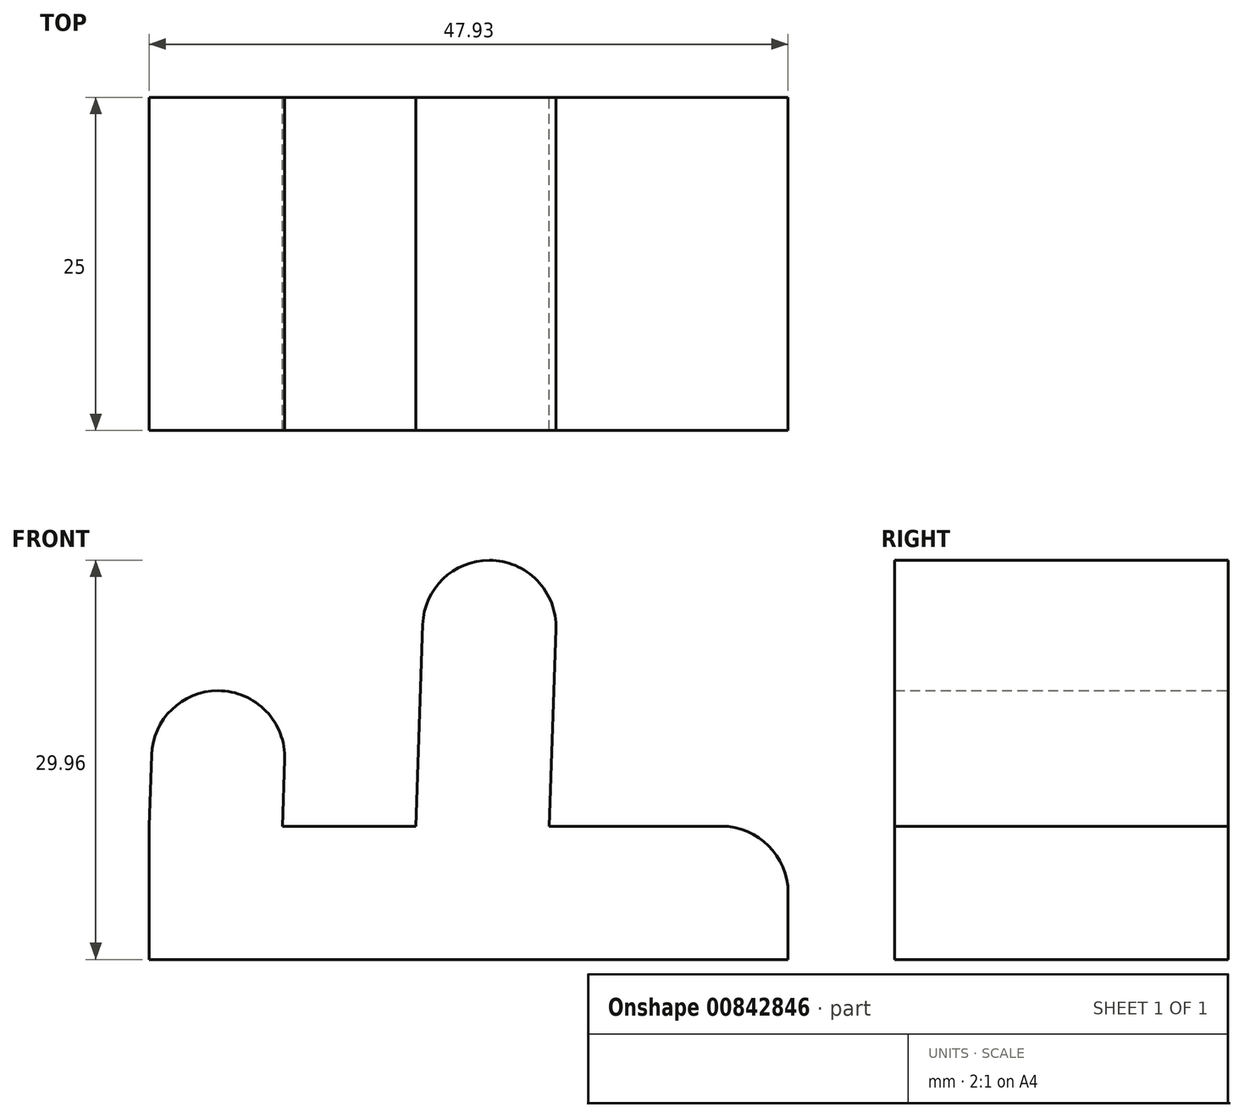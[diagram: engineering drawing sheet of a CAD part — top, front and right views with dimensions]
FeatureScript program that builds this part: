
annotation { "Feature Type Name" : "Feature", "Feature Type Description" : "" }
export const myFeature = defineFeature(function(context is Context, id is Id, definition is map)
    precondition{}
    {
        {
            var Q0;
            Q0=qCreatedBy(makeId("Front.planeOp"),FACE);
            var sketch = newSketch(context, id + "F0", { "sketchPlane" : qUnion([Q0])});
            skPoint(sketch, "E0.middle", {"position": v(0, 0) * mm});
            skLineSegment(sketch, "E1", {"start": v(-30, 3.86) * mm, "end": v(-29.65, 14.02) * mm});
            skLineSegment(sketch, "E2", {"start": v(-29.65, 14.02) * mm, "end": v(-19.65, 14.02) * mm});
            skLineSegment(sketch, "E3", {"start": v(-19.65, 14.02) * mm, "end": v(-20, 3.86) * mm});
            skLineSegment(sketch, "E4", {"start": v(-20, 3.86) * mm, "end": v(-10, 3.86) * mm});
            skLineSegment(sketch, "E5", {"start": v(-10, 3.86) * mm, "end": v(-9.3, 23.82) * mm});
            skLineSegment(sketch, "E6", {"start": v(-9.3, 23.82) * mm, "end": v(0.7, 23.82) * mm});
            skLineSegment(sketch, "E7", {"start": v(0.7, 23.82) * mm, "end": v(0, 3.86) * mm});
            skLineSegment(sketch, "E8.bottom", {"start": v(-30, 3.86) * mm, "end": v(17.93, 3.86) * mm});
            skLineSegment(sketch, "E8.top", {"start": v(-30, -6.14) * mm, "end": v(17.93, -6.14) * mm});
            skLineSegment(sketch, "E8.left", {"start": v(-30, 3.86) * mm, "end": v(-30, -6.14) * mm});
            skLineSegment(sketch, "E8.right", {"start": v(17.93, 3.86) * mm, "end": v(17.93, -6.14) * mm});
            skSolve(sketch);
        }
        {
            var Q0;
            Q0 = qSketchRegion(id + "F0", true);
            extrude(context, id + "F1", {"entities" : qUnion([Q0]), "depth" : 25 * mm, "offsetDistance" : 25 * mm});
        }
        {
            var Q0;
            Q0=makeQuery(id+"F1.opExtrude","SWEPT_EDGE",EDGE,{"disambiguationData":[OSD([sQuery(id+"F0.wireOp",EDGE,"E1"),sQuery(id+"F0.wireOp",EDGE,"E2")])]});
            fillet(context, id + "F2", {"entities" : qUnion([Q0]), "radius" : 5 * mm, "tangentPropagation" : true, "allowEdgeOverflow" : false});
        }
        {
            var Q0;
            Q0=makeQuery(id+"F1.opExtrude","SWEPT_EDGE",EDGE,{"disambiguationData":[OSD([sQuery(id+"F0.wireOp",EDGE,"E2"),sQuery(id+"F0.wireOp",EDGE,"E3")])]});
            var Q1;
            Q1=makeQuery(id+"F1.opExtrude","SWEPT_EDGE",EDGE,{"disambiguationData":[OSD([sQuery(id+"F0.wireOp",EDGE,"E5"),sQuery(id+"F0.wireOp",EDGE,"E6")])]});
            fillet(context, id + "F3", {"entities" : qUnion([Q0, Q1]), "radius" : 5 * mm, "tangentPropagation" : true, "allowEdgeOverflow" : false});
        }
        {
            var Q0;
            Q0=makeQuery(id+"F1.opExtrude","SWEPT_EDGE",EDGE,{"disambiguationData":[OSD([sQuery(id+"F0.wireOp",EDGE,"E6"),sQuery(id+"F0.wireOp",EDGE,"E7")])]});
            fillet(context, id + "F4", {"entities" : qUnion([Q0]), "radius" : 5 * mm, "tangentPropagation" : true, "allowEdgeOverflow" : false});
        }
        {
            var Q0;
            Q0=makeQuery(id+"F1.opExtrude","SWEPT_EDGE",EDGE,{"disambiguationData":[OSD([sQuery(id+"F0.wireOp",EDGE,"E8.bottom"),sQuery(id+"F0.wireOp",EDGE,"E8.right")])]});
            fillet(context, id + "F5", {"entities" : qUnion([Q0]), "radius" : 5 * mm, "tangentPropagation" : true, "allowEdgeOverflow" : false});
        }
    });
